# Revit family: Electronics_Masking-Generators_Biamp_Cambridge_Sound-Masking-System_DS1042__
name_source: partatom
category: Communication Devices
units: mm (PartAtom-declared; Revit-internal decimal feet)

## family parameters
Cut with Voids When Loaded = No
Host = Face
Maintain Annotation Orientation = No
OmniClass Number = 23.85.10.11
OmniClass Title = Audio Information, Sound Signals
Part Type = Normal
Room Calculation Point = No
Round Connector Dimension = Use Diameter
Shared = No

## types (1)
- DS1042
    Apparent Load = 75 VA
    Audio Output Level = 1 - 25 Watts @ 70.7V
    Audio Outputs = 1 - Class 2 Wiring (Stereo or Mono)
    Certifications = UL813
    Connector Description = NEMA 5-15P; 120 VAC 60 Hz (internal), 27 Watts, 3A Fuse
    Default Elevation = 4' - 0"
    Depth = 0' - 8 1/4"
    Description = Dynasound® DS1042 Sound Masking System for Use with 70.7 Volt Speakers
    Height = 0' - 3 1/2"
    Housing Material = Biamp - Plastic - Beige
    Manufacturer = Biamp
    Masking Zones = 1
    Max Power Consumption = 75 W
    Model = DS1042
    Mounting = Supporting/Shelf
    Non Correlated Masking Sources = 1
    Number of Poles = 1
    Output = 25 W, 70.7 V
    Output Connections = Terminal Strip
    Power Factor = 1
    Product Documentation Link = https://downloads.biamp.com
    Product Page URL = https://www.biamp.com
    Product data url = https://www.bimobject.com
    Shipping Weight = 9.00 lbf
    Sound Masking Frequency Response = 160Hz to 5kHz
    Temperature Range = 14 - 104° F (-10 – 40° C)
    Type = Sound masking generator and amplifier
    URL = https://www.biamp.com
    Voltage = 120 V
    Width = 0' - 7 3/4"

## geometry (parser evidence)
native form markers: Sweep x2
no freeform markers — native parametric forms only
